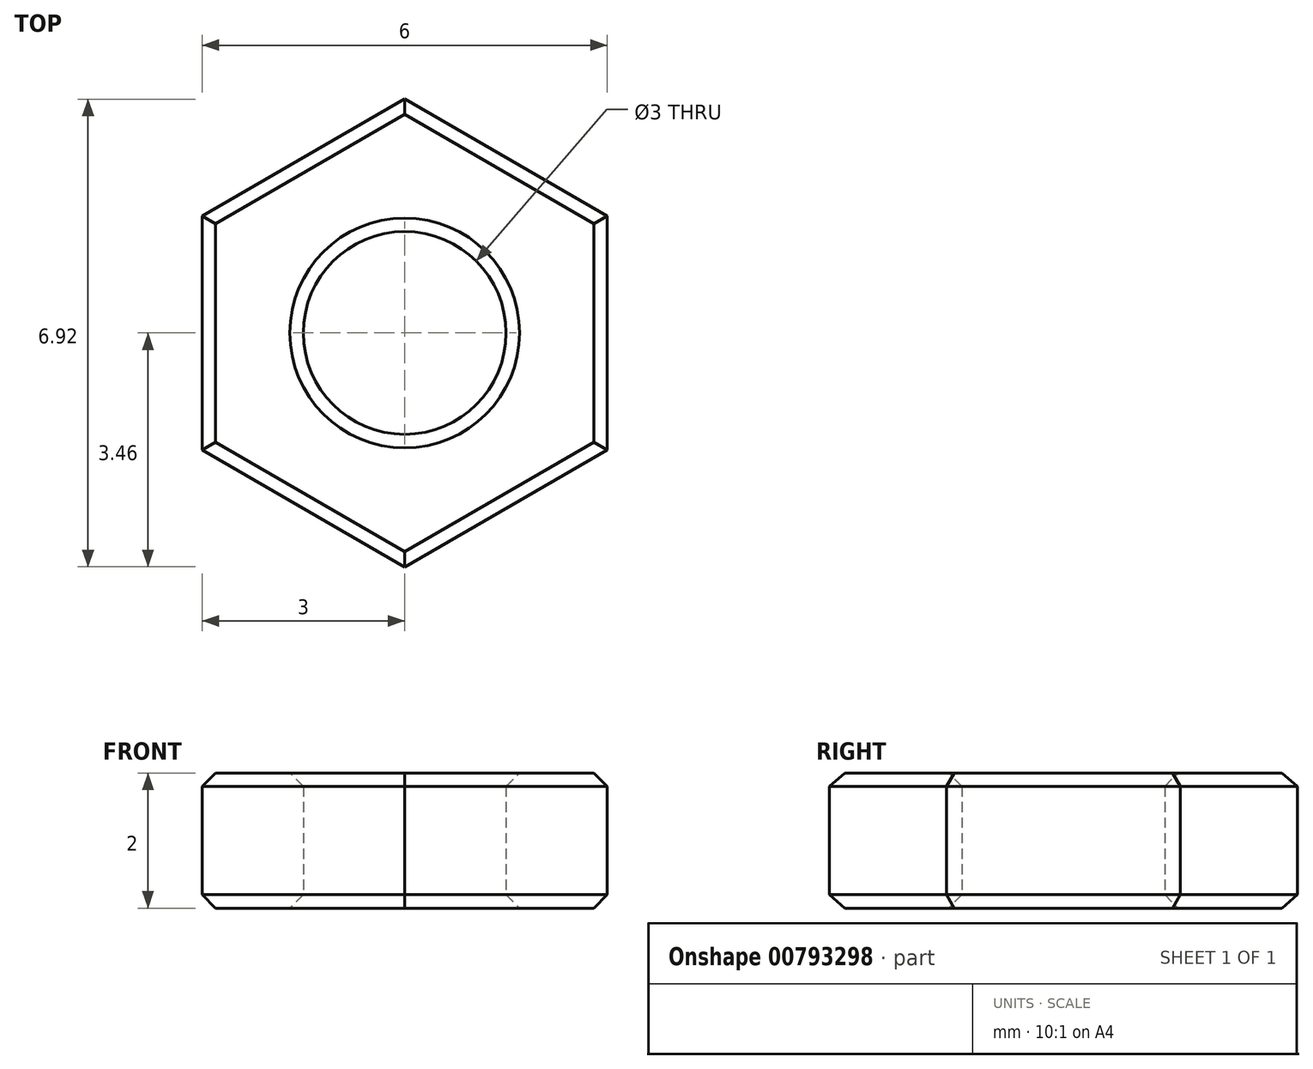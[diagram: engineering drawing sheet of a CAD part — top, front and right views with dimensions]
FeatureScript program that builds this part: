
annotation { "Feature Type Name" : "Feature", "Feature Type Description" : "" }
export const myFeature = defineFeature(function(context is Context, id is Id, definition is map)
    precondition{}
    {
        {
            var Q0;
            Q0=qCreatedBy(makeId("Top.planeOp"),FACE);
            var sketch = newSketch(context, id + "F0", { "sketchPlane" : qUnion([Q0])});
            skCircle(sketch, "E0.cCircle", {"center": v(0, 0) * mm, "radius": 3 * mm, "construction": true});
            skLineSegment(sketch, "E0.0", {"start": v(3, 1.73) * mm, "end": v(3, -1.73) * mm});
            skLineSegment(sketch, "E0.1", {"start": v(3, -1.73) * mm, "end": v(0, -3.46) * mm});
            skLineSegment(sketch, "E0.2", {"start": v(0, -3.46) * mm, "end": v(-3, -1.73) * mm});
            skLineSegment(sketch, "E0.3", {"start": v(-3, -1.73) * mm, "end": v(-3, 1.73) * mm});
            skLineSegment(sketch, "E0.4", {"start": v(-3, 1.73) * mm, "end": v(0, 3.46) * mm});
            skLineSegment(sketch, "E0.5", {"start": v(0, 3.46) * mm, "end": v(3, 1.73) * mm});
            skPoint(sketch, "E0.0.midPoint", {"position": v(3, 0) * mm});
            skCircle(sketch, "E1", {"center": v(0, 0) * mm, "radius": 1.5 * mm});
            skSolve(sketch);
        }
        {
            var Q0;
            Q0 = qSketchRegion(id + "F0", true);
            extrude(context, id + "F1", {"entities" : qUnion([Q0]), "depth" : 2 * mm, "offsetDistance" : 25 * mm});
        }
        {
            var Q0;
            Q0=makeQuery(id+"F1.opExtrude","CAP_FACE",FACE,{"disambiguationData":[OSD([sQuery(id+"F0.wireOp",EDGE,"E0.0"),sQuery(id+"F0.wireOp",EDGE,"E0.1"),sQuery(id+"F0.wireOp",EDGE,"E0.2"),sQuery(id+"F0.wireOp",EDGE,"E0.3"),sQuery(id+"F0.wireOp",EDGE,"E0.4"),sQuery(id+"F0.wireOp",EDGE,"E0.5"),sQuery(id+"F0.wireOp",EDGE,"E1")])],"isStart":false});
            var Q1;
            Q1=makeQuery(id+"F1.opExtrude","CAP_FACE",FACE,{"disambiguationData":[OSD([sQuery(id+"F0.wireOp",EDGE,"E0.0"),sQuery(id+"F0.wireOp",EDGE,"E0.1"),sQuery(id+"F0.wireOp",EDGE,"E0.2"),sQuery(id+"F0.wireOp",EDGE,"E0.3"),sQuery(id+"F0.wireOp",EDGE,"E0.4"),sQuery(id+"F0.wireOp",EDGE,"E0.5"),sQuery(id+"F0.wireOp",EDGE,"E1")])],"isStart":true});
            chamfer(context, id + "F2", {"entities" : qUnion([Q0, Q1]), "width" : 0.2 * mm, "tangentPropagation" : true});
        }
    });
